# Revit family: 873-00-001-DN40-65
name_source: partatom
category: Pipe Accessories
units: mm (PartAtom-declared; Revit-internal decimal feet)

## family parameters
Always vertical = Yes
Cut with Voids When Loaded = No
Part Type = Valve - Breaks Into
Round Connector Dimension = Use Diameter
Shared = No
Work Plane-Based = No

## types (3) — shared parameters
873-0040-00-141000 = DN40_PN16
873-0050-00-141000 = DN50_PN16
873-0065-00-141000 = DN65_PN16
Body_Wallthicknss = 10 mm  [stored 0.0328084 ft]
Description_ = AVK DISMANTLING JOINT
Flange_thickness = 20 mm  [stored 0.0656168 ft]
Search_table = 873-00-001-DN40-65
T = 16 mm  [stored 0.0524934 ft]
URL product pages = https://www.avkvalves.com

## per-type parameters (varying)
| type | A | DN | Id(Radius) | L | d1 | d2 |
| DN40 | 165 mm  [stored 0.541339 ft] | 40 mm  [stored 0.131234 ft] | 20 mm  [stored 0.0656168 ft] | 280 mm  [stored 0.918635 ft] | 110 mm  [stored 0.360892 ft] | 75 mm |
| DN50 | 155 mm  [stored 0.50853 ft] | 50 mm  [stored 0.164042 ft] | 25 mm  [stored 0.082021 ft] | 330 mm  [stored 1.08268 ft] | 125 mm  [stored 0.410105 ft] | 83 mm |
| DN65 | 190 mm  [stored 0.62336 ft] | 65 mm  [stored 0.213255 ft] | 33 mm | 330 mm  [stored 1.08268 ft] | 145 mm  [stored 0.475722 ft] | 93 mm |

note: [stored X ft] marks values corroborated as IEEE doubles in the binary element streams (Revit-internal decimal feet)

## geometry (parser evidence)
native form markers: Sweep x7
no freeform markers — native parametric forms only
